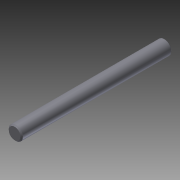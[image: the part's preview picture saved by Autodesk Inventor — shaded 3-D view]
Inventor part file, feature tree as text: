
AUTODESK INVENTOR PART (.ipt)
format: ipt  version: 2013 (Build 170138000, 138)  size: 72,704 bytes
history: native  units: in
note: dims shown in document units (in); Inventor stores cm internally (conversion verified against a paired STEP export)
features: extrude x1, chamfer x1, sketch x1
ambient origin geometry x8: Origin, YZ Plane, XZ Plane, XY Plane, X Axis, Y Axis, Z Axis, Center Point
bodies: Solid1 (feature_tree)
feature tree (3):
  extrude  "Extrusion1"  Depth=0.63in TaperAngle=0.0deg
  chamfer  "Chamfer1"  Distance=0.005in Angle=45.0deg
  sketch  "Sketch1"  dims[d0=0.059in d1=0.63in d2=0.0in d3=0.005in d4=0.125in d5=45.0deg]
